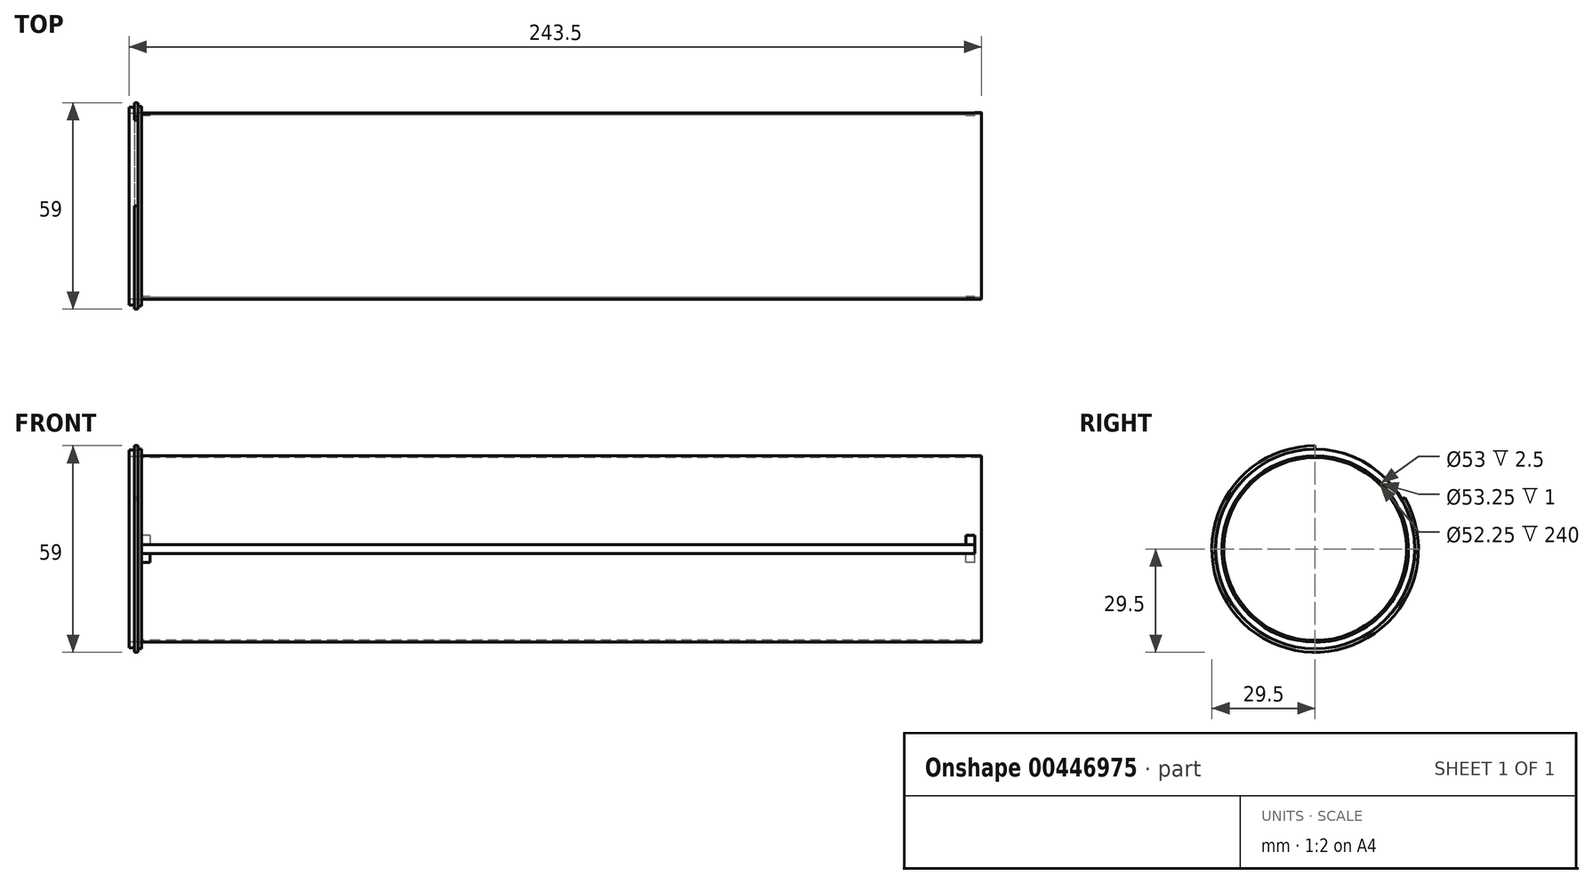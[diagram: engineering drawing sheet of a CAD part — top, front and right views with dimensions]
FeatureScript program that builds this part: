
annotation { "Feature Type Name" : "Feature", "Feature Type Description" : "" }
export const myFeature = defineFeature(function(context is Context, id is Id, definition is map)
    precondition{}
    {
        {
            var Q0;
            Q0=qCreatedBy(makeId("Right.planeOp"),FACE);
            var sketch = newSketch(context, id + "F0", { "sketchPlane" : qUnion([Q0])});
            skCircle(sketch, "E0", {"center": v(0, 0) * mm, "radius": 26.12 * mm});
            skCircle(sketch, "E1", {"center": v(0, 0) * mm, "radius": 26.62 * mm});
            skCircle(sketch, "E2", {"center": v(0, 0) * mm, "radius": 28.5 * mm});
            skSolve(sketch);
        }
        {
            var Q0;
            Q0=makeQuery(id+"F0.imprint","IMPRINT",FACE,{"disambiguationData":[TD([[makeQuery(id+"F0.imprint","IMPRINT",EDGE,{"derivedFrom":sQuery(id+"F0.wireOp",EDGE,"E0")}),-1.0]])]});
            var Q1;
            Q1=sQuery(id+"F0.wireOp",EDGE,"E1");
            var Q2;
            Q2=sQuery(id+"F0.wireOp",EDGE,"E0");
            extrude(context, id + "F1", {"entities" : qUnion([Q0]), "surfaceEntities" : qUnion([Q1, Q2]), "depth" : 240 * mm});
        }
        {
            var Q0;
            Q0=qCreatedBy(makeId("Right.planeOp"),FACE);
            var sketch = newSketch(context, id + "F2", { "sketchPlane" : qUnion([Q0])});
            skLineSegment(sketch, "E3.bottom", {"start": v(-26.62, -1.25) * mm, "end": v(-25.9, -1.25) * mm});
            skLineSegment(sketch, "E3.top", {"start": v(-26.62, 1.25) * mm, "end": v(-25.9, 1.25) * mm});
            skLineSegment(sketch, "E3.left", {"start": v(-26.62, -1.25) * mm, "end": v(-26.62, 1.25) * mm});
            skLineSegment(sketch, "E3.right", {"start": v(-25.9, -1.25) * mm, "end": v(-25.9, 1.25) * mm});
            skPoint(sketch, "E3.middle", {"position": v(-26.26, 0) * mm});
            skLineSegment(sketch, "E4", {"start": v(-26.62, 0) * mm, "end": v(-25.9, 0) * mm});
            skSolve(sketch);
        }
        {
            var Q0;
            Q0 = qSketchRegion(id + "F2", true);
            extrude(context, id + "F3", {"entities" : qUnion([Q0]), "operationType" : NewBodyOperationType.REMOVE, "depth" : 238 * mm});
        }
        {
            var Q0;
            Q0=qCreatedBy(makeId("Right.planeOp"),FACE);
            var sketch = newSketch(context, id + "F4", { "sketchPlane" : qUnion([Q0])});
            skLineSegment(sketch, "E5.bottom", {"start": v(26.62, 1.25) * mm, "end": v(25.96, 1.25) * mm});
            skLineSegment(sketch, "E5.top", {"start": v(26.62, -1.25) * mm, "end": v(25.96, -1.25) * mm});
            skLineSegment(sketch, "E5.left", {"start": v(26.62, 1.25) * mm, "end": v(26.62, -1.25) * mm});
            skLineSegment(sketch, "E5.right", {"start": v(25.96, 1.25) * mm, "end": v(25.96, -1.25) * mm});
            skPoint(sketch, "E5.middle", {"position": v(26.3, 0) * mm});
            skSolve(sketch);
        }
        {
            var Q0;
            Q0=makeQuery(id+"F4.imprint","IMPRINT",FACE,{"disambiguationData":[TD([[makeQuery(id+"F4.imprint","IMPRINT",EDGE,{"derivedFrom":sQuery(id+"F4.wireOp",EDGE,"E5.bottom")}),1.0]])]});
            extrude(context, id + "F5", {"entities" : qUnion([Q0]), "operationType" : NewBodyOperationType.REMOVE, "depth" : 238 * mm});
        }
        {
            var Q0;
            Q0 = qSketchRegion(id + "F0", true);
            extrude(context, id + "F6", {"entities" : qUnion([Q0]), "operationType" : NewBodyOperationType.ADD, "oppositeDirection" : true, "depth" : 1 * mm});
        }
        {
            var Q0;
            Q0=qCreatedBy(makeId("Front.planeOp"),FACE);
            cPlane(context, id + "F7", {"entities" : qUnion([Q0]), "cplaneType" : CPlaneType.OFFSET, "offset" : 53.25 / 2 * mm, "oppositeDirection" : true, "width" : 150 * mm, "height" : 150 * mm});
        }
        {
            var Q0;
            Q0=qCreatedBy(id+"F7.planeOp",FACE);
            var sketch = newSketch(context, id + "F8", { "sketchPlane" : qUnion([Q0])});
            skLineSegment(sketch, "E6.bottom", {"start": v(238, -1.25) * mm, "end": v(235.5, -1.25) * mm});
            skLineSegment(sketch, "E6.top", {"start": v(238, -3.85) * mm, "end": v(235.5, -3.85) * mm});
            skLineSegment(sketch, "E6.left", {"start": v(238, -1.25) * mm, "end": v(238, -3.85) * mm});
            skLineSegment(sketch, "E6.right", {"start": v(235.5, -1.25) * mm, "end": v(235.5, -3.85) * mm});
            skLineSegment(sketch, "E7.bottom", {"start": v(2.5, 1.25) * mm, "end": v(0, 1.25) * mm});
            skLineSegment(sketch, "E7.top", {"start": v(2.5, 3.85) * mm, "end": v(0, 3.85) * mm});
            skLineSegment(sketch, "E7.left", {"start": v(2.5, 1.25) * mm, "end": v(2.5, 3.85) * mm});
            skLineSegment(sketch, "E7.right", {"start": v(0, 1.25) * mm, "end": v(0, 3.85) * mm});
            skSolve(sketch);
        }
        {
            var Q0;
            Q0=makeQuery(id+"F8.imprint","IMPRINT",FACE,{"disambiguationData":[TD([[makeQuery(id+"F8.imprint","IMPRINT",EDGE,{"derivedFrom":sQuery(id+"F8.wireOp",EDGE,"E6.bottom")}),1.0]])]});
            extrude(context, id + "F9", {"entities" : qUnion([Q0]), "operationType" : NewBodyOperationType.REMOVE, "depth" : 2 * mm});
        }
        {
            var Q0;
            Q0=qCreatedBy(makeId("Front.planeOp"),FACE);
            cPlane(context, id + "F10", {"entities" : qUnion([Q0]), "cplaneType" : CPlaneType.OFFSET, "offset" : (53.25 / 2) * mm, "width" : 150 * mm, "height" : 150 * mm});
        }
        {
            var Q0;
            Q0=qCreatedBy(id+"F10.planeOp",FACE);
            var sketch = newSketch(context, id + "F11", { "sketchPlane" : qUnion([Q0])});
            skLineSegment(sketch, "E8.bottom", {"start": v(2.5, -1.25) * mm, "end": v(0, -1.25) * mm});
            skLineSegment(sketch, "E8.top", {"start": v(2.5, -3.85) * mm, "end": v(0, -3.85) * mm});
            skLineSegment(sketch, "E8.left", {"start": v(2.5, -1.25) * mm, "end": v(2.5, -3.85) * mm});
            skLineSegment(sketch, "E8.right", {"start": v(0, -1.25) * mm, "end": v(0, -3.85) * mm});
            skLineSegment(sketch, "E9.bottom", {"start": v(238, 1.25) * mm, "end": v(235.5, 1.25) * mm});
            skLineSegment(sketch, "E9.top", {"start": v(238, 3.85) * mm, "end": v(235.5, 3.85) * mm});
            skLineSegment(sketch, "E9.left", {"start": v(238, 1.25) * mm, "end": v(238, 3.85) * mm});
            skLineSegment(sketch, "E9.right", {"start": v(235.5, 1.25) * mm, "end": v(235.5, 3.85) * mm});
            skSolve(sketch);
        }
        {
            var Q0;
            Q0=makeQuery(id+"F11.imprint","IMPRINT",FACE,{"disambiguationData":[TD([[makeQuery(id+"F11.imprint","IMPRINT",EDGE,{"derivedFrom":sQuery(id+"F11.wireOp",EDGE,"E8.bottom")}),1.0]])]});
            extrude(context, id + "F12", {"entities" : qUnion([Q0]), "operationType" : NewBodyOperationType.REMOVE, "oppositeDirection" : true, "depth" : 2 * mm});
        }
        {
            var Q0;
            Q0=makeQuery(id+"F11.imprint","IMPRINT",FACE,{"disambiguationData":[TD([[makeQuery(id+"F11.imprint","IMPRINT",EDGE,{"derivedFrom":sQuery(id+"F11.wireOp",EDGE,"E9.bottom")}),-1.0]])]});
            extrude(context, id + "F13", {"entities" : qUnion([Q0]), "operationType" : NewBodyOperationType.REMOVE, "oppositeDirection" : true, "depth" : 2 * mm});
        }
        {
            var Q0;
            Q0=makeQuery(id+"F8.imprint","IMPRINT",FACE,{"disambiguationData":[TD([[makeQuery(id+"F8.imprint","IMPRINT",EDGE,{"derivedFrom":sQuery(id+"F8.wireOp",EDGE,"E7.bottom")}),-1.0]])]});
            extrude(context, id + "F14", {"entities" : qUnion([Q0]), "operationType" : NewBodyOperationType.REMOVE, "depth" : 2 * mm});
        }
        {
            var Q0;
            Q0=makeQuery(id+"F6.opExtrude","CAP_FACE",FACE,{"disambiguationData":[OSD([sQuery(id+"F0.wireOp",EDGE,"E1"),sQuery(id+"F0.wireOp",EDGE,"E2")])],"isStart":false});
            var sketch = newSketch(context, id + "F15", { "sketchPlane" : qUnion([Q0])});
            skCircle(sketch, "E10", {"center": v(0, 0) * mm, "radius": 26.5 * mm});
            skCircle(sketch, "E11", {"center": v(0, 0) * mm, "radius": 28.25 * mm});
            skSolve(sketch);
        }
        {
            var Q0;
            Q0=makeQuery(id+"F15.imprint","IMPRINT",FACE,{"disambiguationData":[TD([[makeQuery(id+"F15.imprint","IMPRINT",EDGE,{"derivedFrom":sQuery(id+"F15.wireOp",EDGE,"E11")}),1.0]])]});
            var sketch = newSketch(context, id + "F16", { "sketchPlane" : qUnion([Q0])});
            skCircle(sketch, "E12", {"center": v(0, 0) * mm, "radius": 26.5 * mm});
            skCircle(sketch, "E13", {"center": v(0, 0) * mm, "radius": 29.5 * mm});
            skSolve(sketch);
        }
        {
            var Q0;
            Q0 = qSketchRegion(id + "F16", true);
            extrude(context, id + "F17", {"entities" : qUnion([Q0]), "operationType" : NewBodyOperationType.ADD, "depth" : 1 * mm});
        }
        {
            var Q0;
            Q0=makeQuery(id+"F17.opExtrude","CAP_FACE",FACE,{"disambiguationData":[OSD([sQuery(id+"F16.wireOp",EDGE,"E12"),sQuery(id+"F16.wireOp",EDGE,"E13")])],"isStart":false});
            var sketch = newSketch(context, id + "F18", { "sketchPlane" : qUnion([Q0])});
            skCircle(sketch, "E14.cCircle", {"center": v(0, 0) * mm, "radius": 38.3 * mm, "construction": true});
            skLineSegment(sketch, "E14.0", {"start": v(38.3, 22.12) * mm, "end": v(38.3, -22.12) * mm});
            skLineSegment(sketch, "E14.1", {"start": v(38.3, -22.12) * mm, "end": v(0, -44.23) * mm});
            skLineSegment(sketch, "E14.2", {"start": v(0, -44.23) * mm, "end": v(-38.3, -22.12) * mm});
            skLineSegment(sketch, "E14.3", {"start": v(-38.3, -22.12) * mm, "end": v(-38.3, 22.12) * mm});
            skLineSegment(sketch, "E14.4", {"start": v(-38.3, 22.12) * mm, "end": v(0, 44.23) * mm});
            skLineSegment(sketch, "E14.5", {"start": v(0, 44.23) * mm, "end": v(38.3, 22.12) * mm});
            skPoint(sketch, "E14.0.midPoint", {"position": v(38.3, 0) * mm});
            skLineSegment(sketch, "E15", {"start": v(0, 44.23) * mm, "end": v(0, -44.23) * mm});
            skLineSegment(sketch, "E16", {"start": v(-38.3, 22.12) * mm, "end": v(38.3, -22.12) * mm});
            skLineSegment(sketch, "E17", {"start": v(-38.3, -22.12) * mm, "end": v(0, 0) * mm});
            skLineSegment(sketch, "E18", {"start": v(38.3, 22.12) * mm, "end": v(0, 0) * mm});
            skSolve(sketch);
        }
        {
            var Q0;
            {var subQ0=sQuery(id+"F18.wireOp",EDGE,"E15");var subQ1=makeQuery(id+"F17.opExtrude","CAP_EDGE",EDGE,{"disambiguationData":[OSD([sQuery(id+"F16.wireOp",EDGE,"E13")])],"isStart":false});var subQ2=makeQuery(id+"F18.imprint","INTERSECT",VERTEX,{"disambiguationData":[OD(0.0)],"derivedFrom":[subQ1,subQ0]});Q0=makeQuery(id+"F18.imprint","IMPRINT",FACE,{"disambiguationData":[TD([[makeQuery(id+"F18.imprint","IMPRINT",EDGE,{"disambiguationData":[TD([[subQ2,-1.0]])],"derivedFrom":subQ0}),-1.0]])]});}
            var Q1;
            {var subQ0=sQuery(id+"F18.wireOp",EDGE,"E16");var subQ1=makeQuery(id+"F17.opExtrude","CAP_EDGE",EDGE,{"disambiguationData":[OSD([sQuery(id+"F16.wireOp",EDGE,"E12")])],"isStart":false});var subQ2=makeQuery(id+"F18.imprint","INTERSECT",VERTEX,{"disambiguationData":[OD(1.0)],"derivedFrom":[subQ1,subQ0]});Q1=makeQuery(id+"F18.imprint","IMPRINT",FACE,{"disambiguationData":[TD([[makeQuery(id+"F18.imprint","IMPRINT",EDGE,{"disambiguationData":[TD([[subQ2,-1.0]])],"derivedFrom":subQ0}),1.0]])]});}
            var Q2;
            {var subQ0=sQuery(id+"F18.wireOp",EDGE,"E15");var subQ1=makeQuery(id+"F17.opExtrude","CAP_EDGE",EDGE,{"disambiguationData":[OSD([sQuery(id+"F16.wireOp",EDGE,"E12")])],"isStart":false});var subQ2=makeQuery(id+"F18.imprint","INTERSECT",VERTEX,{"disambiguationData":[OD(1.0)],"derivedFrom":[subQ1,subQ0]});Q2=makeQuery(id+"F18.imprint","IMPRINT",FACE,{"disambiguationData":[TD([[makeQuery(id+"F18.imprint","IMPRINT",EDGE,{"disambiguationData":[TD([[subQ2,-1.0]])],"derivedFrom":subQ0}),-1.0]])]});}
            extrude(context, id + "F19", {"entities" : qUnion([Q0, Q1, Q2]), "operationType" : NewBodyOperationType.REMOVE, "oppositeDirection" : true, "depth" : 1 * mm});
        }
        {
            var Q0;
            Q0 = qSketchRegion(id + "F15", true);
            extrude(context, id + "F20", {"entities" : qUnion([Q0]), "operationType" : NewBodyOperationType.ADD, "depth" : 2.5 * mm});
        }
    });
